# Revit family: 0047441 Lighting Fixture_Sylvania_Start Flat Panel LED_Surface Mounted
name_source: partatom
category: Lighting Fixtures
revit_build: Autodesk Revit 2016 (Build: 20150220_1215(x64)
units: mm (PartAtom-declared; Revit-internal decimal feet)

## family parameters
Cut with Voids When Loaded = No
Host = Face
Light Source = Yes
OmniClass Number = 23.80.70.11.17
OmniClass Title = Specialized Lighting by Location or Use
Part Type = Normal
Room Calculation Point = No
Round Connector Dimension = Use Diameter
Shared = No

## types (1)
- Start Flat PanelLED 600 WW 3000K
    Apparent Load = 46 VA
    Assembly Code = D5020200
    Body Material = Metal_Sylvania_Startflat Panel LED_White
    CRI (Ra) = 84
    Catalog Number = 0047441 Start Flat PanelLED 600 WW 3000K
    Color Filter = 16777215
    Default Elevation = 0 mm  [stored 0 ft]
    Description = Ultra thin LED Panel, excellent uniformity of light, perfect for ceilings with low voids, high efficacy.Ulta thin edgelit LED 600x600mm Panel with, excellent uniform light distribution. Acrylic PMMA diffuser optimising light output whilst reducing glare. 4239lm 93lm/W.
    Diffuser Material = Polycarbonate_Sylvania_Startflat Panel LED_Opal
    Dimming Lamp Color Temperature Shift = <None>
    Drive Current = 1200mA
    Electrical Protection = CLASS II
    Emit Shape Visible in Rendering = No
    Emit from Rectangle Length = 545 mm
    Emit from Rectangle Width = 545 mm
    Energy Class = A++, A+, A
    Frame Inner Length = 574 mm
    Frame Inner Width = 574 mm
    Glare Control = UGR <25
    Glow Wire Test = 650 °C
    Height = 50 mm  [stored 0.164042 ft]
    IP Rating = IP20
    LOR = 100 %
    Lamp = Integrated LED
    Length = 602 mm
    Life = 50 000h
    Manufacturer = Feilo-Sylvania Group
    Model = Start Flat PanelLED 600 WW 3000K
    Mounting Material = Metal_Sylvania_Startflat Panel LED_Silver
    Panel Length = 595 mm
    Panel Width = 595 mm
    Photometric Web File = 0047441_StartFlatPanelLED600WW3000K-191306.ies
    Product Family = STARTFLAT PANEL LED
    Ta Rating = -15°C to +45°C
    Tilt Angle = -90.00°
    Voltage = 230 V
    Voltage Comments = UNV (Universal Voltage; 220-240 Volt)
    Weight = 3.00 kg
    Width = 602 mm

note: [stored X ft] marks values corroborated as IEEE doubles in the binary element streams (Revit-internal decimal feet)

## geometry (parser evidence)
native form markers: Blend x4, Sweep x2
no freeform markers — native parametric forms only
